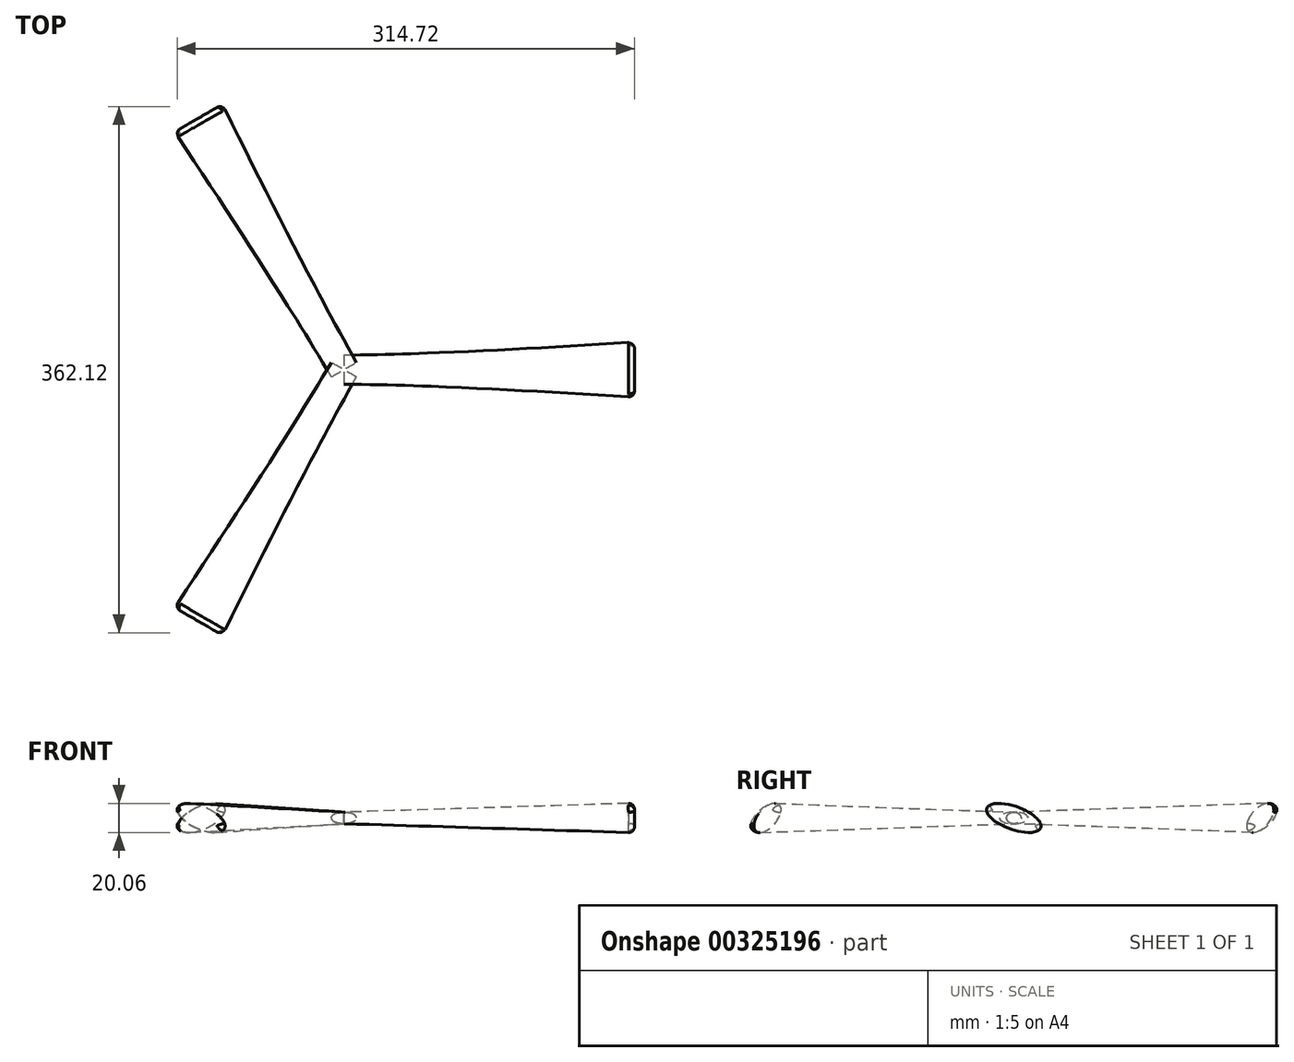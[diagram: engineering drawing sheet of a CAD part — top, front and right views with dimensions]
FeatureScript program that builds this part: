
annotation { "Feature Type Name" : "Feature", "Feature Type Description" : "" }
export const myFeature = defineFeature(function(context is Context, id is Id, definition is map)
    precondition{}
    {
        {
            var Q0;
            Q0=qCreatedBy(makeId("Right.planeOp"),FACE);
            var sketch = newSketch(context, id + "F0", { "sketchPlane" : qUnion([Q0])});
            skEllipse(sketch, "E0", {"center": v(0, 0) * mm, "majorRadius": 10 * mm, "minorRadius": 4 * mm, "majorAxis": v(1, 0)});
            skSolve(sketch);
        }
        {
            var Q0;
            Q0=qCreatedBy(makeId("Right.planeOp"),FACE);
            cPlane(context, id + "F1", {"entities" : qUnion([Q0]), "cplaneType" : CPlaneType.OFFSET, "offset" : 200 * mm, "width" : 150 * mm, "height" : 150 * mm});
        }
        {
            var Q0;
            Q0=qCreatedBy(id+"F1.planeOp",FACE);
            var sketch = newSketch(context, id + "F2", { "sketchPlane" : qUnion([Q0])});
            skLineSegment(sketch, "E1", {"start": v(0, 0) * mm, "end": v(87.44, -31.83) * mm, "construction": true});
            skEllipse(sketch, "E2", {"center": v(0, 0) * mm, "majorRadius": 20 * mm, "minorRadius": 8 * mm, "majorAxis": v(0.94, -0.34)});
            skPoint(sketch, "E3", {"position": v(18.8, -6.84) * mm});
            skSolve(sketch);
        }
        {
            var Q0;
            Q0=makeQuery(id+"F0.imprint","IMPRINT",FACE,{"disambiguationData":[TD([[makeQuery(id+"F0.imprint","IMPRINT",EDGE,{"derivedFrom":sQuery(id+"F0.wireOp",EDGE,"E0")}),1.0]])]});
            var Q1;
            Q1=makeQuery(id+"F2.imprint","IMPRINT",FACE,{"disambiguationData":[TD([[makeQuery(id+"F2.imprint","IMPRINT",EDGE,{"derivedFrom":sQuery(id+"F2.wireOp",EDGE,"E2")}),1.0]])]});
            loft(context, id + "F3", {"sheetProfilesArray" : [{ "sheetProfileEntities" : qUnion([Q0]) }, { "sheetProfileEntities" : qUnion([Q1]) }]});
        }
        {
            var Q0;
            Q0=makeQuery(id+"F3.opLoft","MID_CAP_EDGE",EDGE,{"disambiguationData":[OSD([sQuery(id+"F0.wireOp",EDGE,"E0"),sQuery(id+"F2.wireOp",EDGE,"E2")])],"capPos":1.0});
            fillet(context, id + "F4", {"entities" : qUnion([Q0]), "radius" : 4 * mm, "tangentPropagation" : true, "allowEdgeOverflow" : false});
        }
        {
            var Q0;
            Q0=qCreatedBy(makeId("Right.planeOp"),FACE);
            var sketch = newSketch(context, id + "F5", { "sketchPlane" : qUnion([Q0])});
            skLineSegment(sketch, "E4", {"start": v(0, 0) * mm, "end": v(0, 152.48) * mm});
            skSolve(sketch);
        }
        {
            var Q0;
            Q0=makeQuery(id+"F3.opLoft","SWEPT_BODY",BODY,{"disambiguationData":[OSD([makeQuery(id+"F0.imprint","IMPRINT",FACE,{"disambiguationData":[TD([[makeQuery(id+"F0.imprint","IMPRINT",EDGE,{"derivedFrom":sQuery(id+"F0.wireOp",EDGE,"E0")}),1.0]])]}),makeQuery(id+"F2.imprint","IMPRINT",FACE,{"disambiguationData":[TD([[makeQuery(id+"F2.imprint","IMPRINT",EDGE,{"derivedFrom":sQuery(id+"F2.wireOp",EDGE,"E2")}),1.0]])]})])]});
            var Q1;
            Q1=sQuery(id+"F5.wireOp",EDGE,"E4");
            circularPattern(context, id + "F6", {"entities" : qUnion([Q0]), "axis" : qUnion([Q1]), "angle" : 360 * degree, "instanceCount" : 3, "equalSpace" : true});
        }
    });
